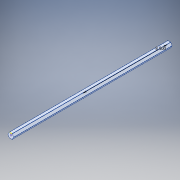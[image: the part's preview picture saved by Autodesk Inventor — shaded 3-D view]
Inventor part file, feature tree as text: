
AUTODESK INVENTOR PART (.ipt)
format: ipt  version: 2017 (Build 210142000, 142)  size: 138,240 bytes
history: native  units: in
note: dims shown in document units (in); Inventor stores cm internally (conversion verified against a paired STEP export)
features: sketch x4, split x1, fillet x1
ambient origin geometry x8: Origin, YZ Plane, XZ Plane, XY Plane, X Axis, Y Axis, Z Axis, Center Point
bodies: Solid1 (feature_tree)
feature tree (6):
  sketch  "Sketch1"  dims[d3=8.5in]
  split  "Split1"
  sketch  "Sketch3"
  sketch  "Sketch4"
  sketch  "Sketch2"
  fillet  "Fillet1"  Radius=16.0in
